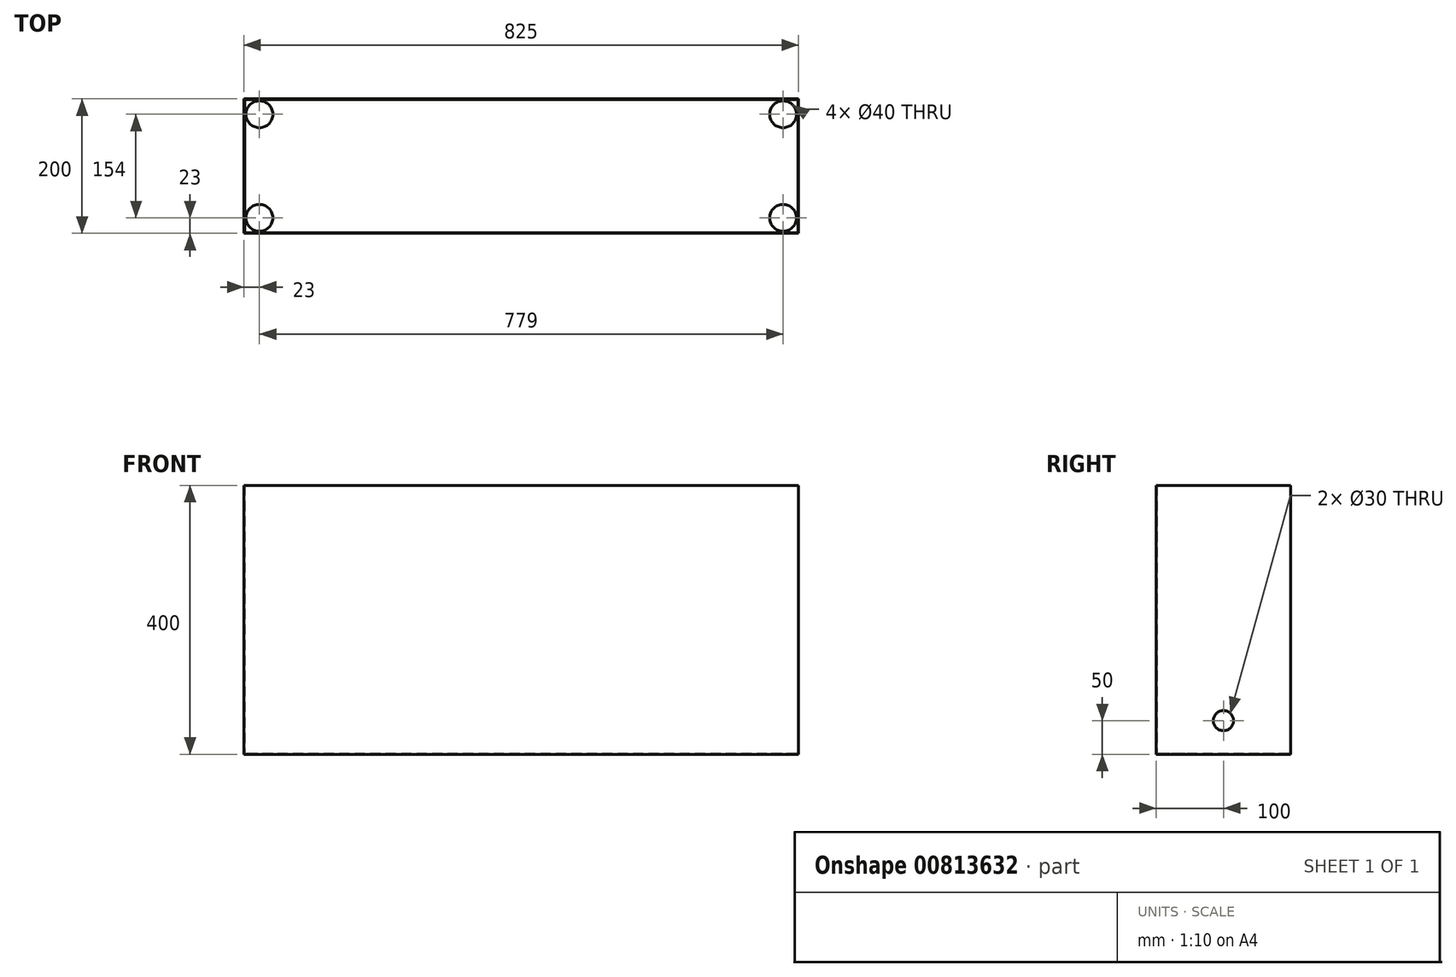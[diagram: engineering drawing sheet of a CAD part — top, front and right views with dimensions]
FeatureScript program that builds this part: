
annotation { "Feature Type Name" : "Feature", "Feature Type Description" : "" }
export const myFeature = defineFeature(function(context is Context, id is Id, definition is map)
    precondition{}
    {
        {
            var Q0;
            Q0=qCreatedBy(makeId("Top.planeOp"),FACE);
            var sketch = newSketch(context, id + "F0", { "sketchPlane" : qUnion([Q0])});
            skLineSegment(sketch, "E0.bottom", {"start": v(412.5, 100) * mm, "end": v(-412.5, 100) * mm});
            skLineSegment(sketch, "E0.top", {"start": v(412.5, -100) * mm, "end": v(-412.5, -100) * mm});
            skLineSegment(sketch, "E0.left", {"start": v(412.5, 100) * mm, "end": v(412.5, -100) * mm});
            skLineSegment(sketch, "E0.right", {"start": v(-412.5, 100) * mm, "end": v(-412.5, -100) * mm});
            skPoint(sketch, "E0.middle", {"position": v(0, 0) * mm});
            skSolve(sketch);
        }
        {
            var Q0;
            Q0=makeQuery(id+"F0.imprint","IMPRINT",FACE,{"disambiguationData":[TD([[makeQuery(id+"F0.imprint","IMPRINT",EDGE,{"derivedFrom":sQuery(id+"F0.wireOp",EDGE,"E0.bottom")}),1.0]])]});
            extrude(context, id + "F1", {"entities" : qUnion([Q0]), "depth" : 400 * mm, "offsetDistance" : 25 * mm});
        }
        {
            var Q0;
            Q0=makeQuery(id+"F1.opExtrude","CAP_FACE",FACE,{"disambiguationData":[OSD([sQuery(id+"F0.wireOp",EDGE,"E0.bottom"),sQuery(id+"F0.wireOp",EDGE,"E0.top"),sQuery(id+"F0.wireOp",EDGE,"E0.left"),sQuery(id+"F0.wireOp",EDGE,"E0.right")])],"isStart":false});
            shell(context, id + "F2", {"entities" : qUnion([Q0]), "thickness" : 1 * mm});
        }
        {
            var Q0;
            Q0=makeQuery(id+"F2.opShell","OFFSET_FACE",FACE,{"disambiguationData":[OSD([sQuery(id+"F0.wireOp",EDGE,"E0.bottom"),sQuery(id+"F0.wireOp",EDGE,"E0.top"),sQuery(id+"F0.wireOp",EDGE,"E0.left"),sQuery(id+"F0.wireOp",EDGE,"E0.right")])]});
            var sketch = newSketch(context, id + "F3", { "sketchPlane" : qUnion([Q0])});
            skCircle(sketch, "E1", {"center": v(-389.5, 77) * mm, "radius": 21.5 * mm});
            skCircle(sketch, "E2", {"center": v(-389.5, 77) * mm, "radius": 15.6 * mm});
            skCircle(sketch, "E3", {"center": v(389.5, 77) * mm, "radius": 22 * mm});
            skCircle(sketch, "E4.0", {"center": v(389.5, 77) * mm, "radius": 22.25 * mm});
            skCircle(sketch, "E5.0", {"center": v(389.5, 77) * mm, "radius": 18 * mm});
            skCircle(sketch, "E6", {"center": v(-389.5, -77) * mm, "radius": 22 * mm});
            skCircle(sketch, "E7.0", {"center": v(-389.5, -77) * mm, "radius": 18 * mm});
            skCircle(sketch, "E8", {"center": v(389.5, -77) * mm, "radius": 22 * mm});
            skCircle(sketch, "E9.0", {"center": v(389.5, -77) * mm, "radius": 18 * mm});
            skSolve(sketch);
        }
        {
            var Q0;
            Q0=sQuery(id+"F3.wireOp",EDGE,"E1");
            var Q1;
            Q1=sQuery(id+"F3.wireOp",EDGE,"E2");
            var Q2;
            Q2=sQuery(id+"F3.wireOp",EDGE,"E6");
            var Q3;
            Q3=sQuery(id+"F3.wireOp",EDGE,"E7.0");
            var Q4;
            Q4=sQuery(id+"F3.wireOp",EDGE,"E8");
            var Q5;
            Q5=sQuery(id+"F3.wireOp",EDGE,"E9.0");
            var Q6;
            Q6=sQuery(id+"F3.wireOp",EDGE,"E5.0");
            var Q7;
            Q7=sQuery(id+"F3.wireOp",EDGE,"E3");
            extrude(context, id + "F4", {"bodyType" : ToolBodyType.SURFACE, "surfaceEntities" : qUnion([Q0, Q1, Q2, Q3, Q4, Q5, Q6, Q7]), "depth" : 400 * mm, "offsetDistance" : 25 * mm});
        }
        {
            var Q0;
            Q0=sQuery(id+"F3.wireOp",VERTEX,"E4.0.center");
            var Q1;
            Q1=sQuery(id+"F3.wireOp",VERTEX,"E9.0.center");
            var Q2;
            Q2=sQuery(id+"F3.wireOp",VERTEX,"E1.center");
            var Q3;
            Q3=sQuery(id+"F3.wireOp",VERTEX,"E7.0.center");
            var Q4;
            Q4=makeQuery(id+"F1.opExtrude","SWEPT_BODY",BODY,{"disambiguationData":[OSD([sQuery(id+"F0.wireOp",EDGE,"E0.bottom"),sQuery(id+"F0.wireOp",EDGE,"E0.top"),sQuery(id+"F0.wireOp",EDGE,"E0.left"),sQuery(id+"F0.wireOp",EDGE,"E0.right")])]});
            hole(context, id + "F5", {"style" : HoleStyle.SIMPLE, "endStyle" : HoleEndStyle.THROUGH, "holeDiameter" : 40 * mm, "majorDiameter" : 5 * mm, "isTappedThrough" : true, "tappedDepth" : 12 * mm, "tapClearance" : 3, "locations" : qUnion([Q0, Q1, Q2, Q3]), "scope" : qUnion([Q4])});
        }
        {
            var Q0;
            Q0=makeQuery(id+"F1.opExtrude","SWEPT_FACE",FACE,{"disambiguationData":[OSD([sQuery(id+"F0.wireOp",EDGE,"E0.right")])]});
            var sketch = newSketch(context, id + "F6", { "sketchPlane" : qUnion([Q0])});
            skCircle(sketch, "E10", {"center": v(0, 50) * mm, "radius": 15 * mm});
            skCircle(sketch, "E11.0", {"center": v(0, 50) * mm, "radius": 15.25 * mm});
            skSolve(sketch);
        }
        {
            var Q0;
            Q0=sQuery(id+"F6.wireOp",VERTEX,"E11.0.center");
            var Q1;
            Q1=makeQuery(id+"F1.opExtrude","SWEPT_BODY",BODY,{"disambiguationData":[OSD([sQuery(id+"F0.wireOp",EDGE,"E0.bottom"),sQuery(id+"F0.wireOp",EDGE,"E0.top"),sQuery(id+"F0.wireOp",EDGE,"E0.left"),sQuery(id+"F0.wireOp",EDGE,"E0.right")])]});
            hole(context, id + "F7", {"style" : HoleStyle.SIMPLE, "endStyle" : HoleEndStyle.THROUGH, "holeDiameter" : 30 * mm, "majorDiameter" : 5 * mm, "isTappedThrough" : true, "tappedDepth" : 12 * mm, "tapClearance" : 3, "locations" : qUnion([Q0]), "scope" : qUnion([Q1])});
        }
    });
